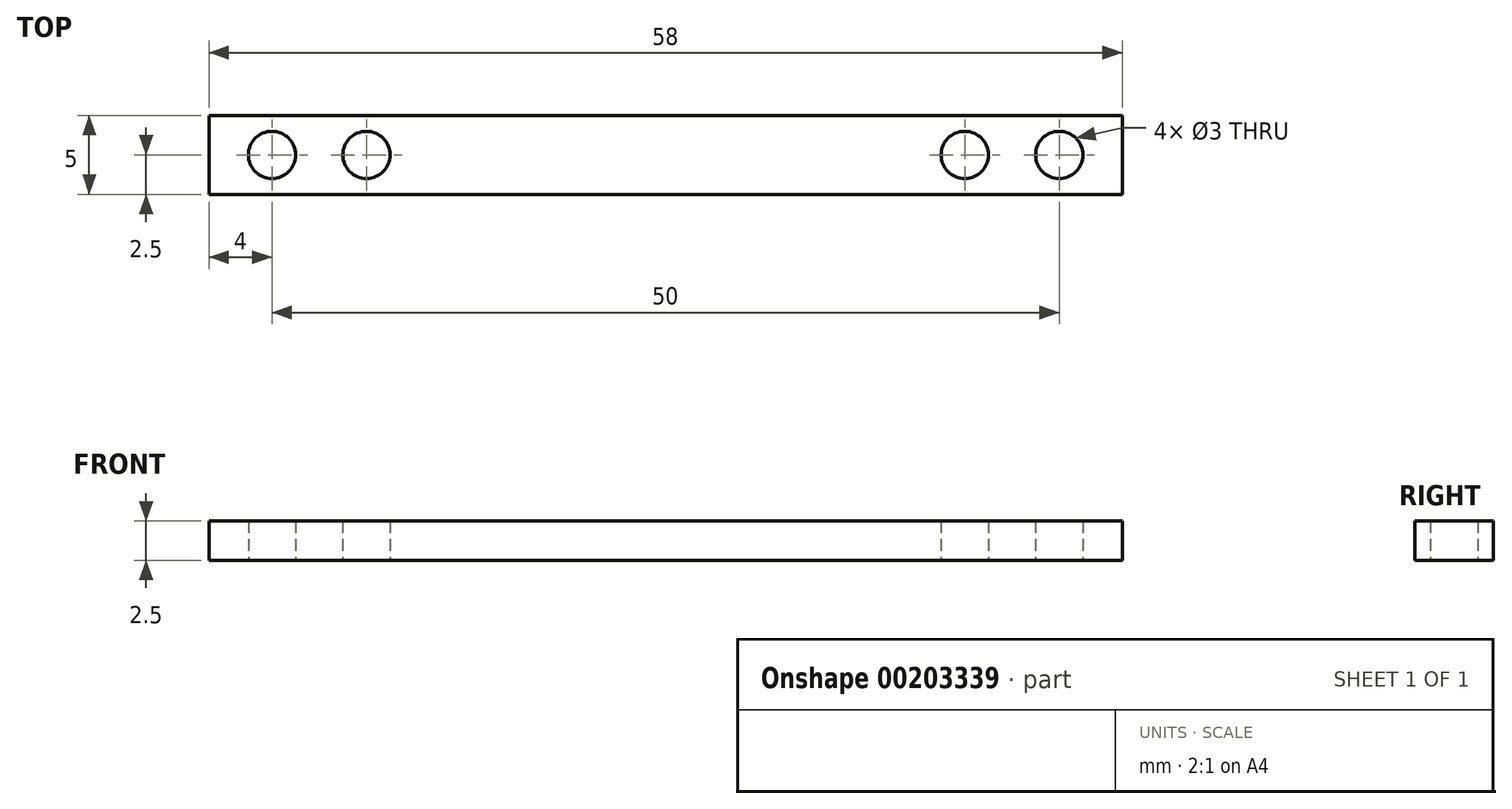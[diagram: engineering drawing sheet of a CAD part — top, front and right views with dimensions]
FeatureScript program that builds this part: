
annotation { "Feature Type Name" : "Feature", "Feature Type Description" : "" }
export const myFeature = defineFeature(function(context is Context, id is Id, definition is map)
    precondition{}
    {
        {
            var Q0;
            Q0=qCreatedBy(makeId("Top.planeOp"),FACE);
            var sketch = newSketch(context, id + "F0", { "sketchPlane" : qUnion([Q0])});
            skLineSegment(sketch, "E0.bottom", {"start": v(29, -2.5) * mm, "end": v(-29, -2.5) * mm});
            skLineSegment(sketch, "E0.top", {"start": v(29, 2.5) * mm, "end": v(-29, 2.5) * mm});
            skLineSegment(sketch, "E0.left", {"start": v(29, -2.5) * mm, "end": v(29, 2.5) * mm});
            skLineSegment(sketch, "E0.right", {"start": v(-29, -2.5) * mm, "end": v(-29, 2.5) * mm});
            skPoint(sketch, "E0.middle", {"position": v(0, 0) * mm});
            skCircle(sketch, "E1", {"center": v(-25, 0) * mm, "radius": 1.5 * mm});
            skLineSegment(sketch, "E2", {"start": v(0, 2.5) * mm, "end": v(0, -2.5) * mm, "construction": true});
            skCircle(sketch, "E3.MirrorC", {"center": v(25, 0) * mm, "radius": 1.5 * mm});
            skCircle(sketch, "E4", {"center": v(-19, 0) * mm, "radius": 1.5 * mm});
            skCircle(sketch, "E5.MirrorC", {"center": v(19, 0) * mm, "radius": 1.5 * mm});
            skSolve(sketch);
        }
        {
            var Q0;
            Q0 = qSketchRegion(id + "F0", true);
            extrude(context, id + "F1", {"entities" : qUnion([Q0]), "depth" : 2.5 * mm});
        }
    });
